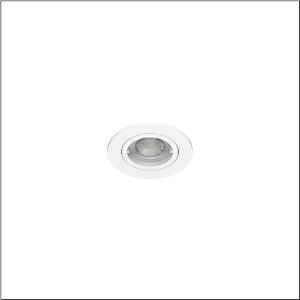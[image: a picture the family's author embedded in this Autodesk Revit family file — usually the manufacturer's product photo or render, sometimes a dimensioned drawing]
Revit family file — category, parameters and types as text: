
# Revit family: lunis_41_spot_51dt137a32a
name_source: partatom
category: Lighting Fixtures
units: mm (PartAtom-declared; Revit-internal decimal feet)

## family parameters
Cut with Voids When Loaded = No
Host = Face
Light Source = No
Part Type = Normal
Room Calculation Point = No
Round Connector Dimension = Use Diameter
Shared = No

## types (1)
- Lunis 41 Spot (1 x LED, 650 lm, 6.5 W, 3000K)
    Apparent Load = 7 VA
    CIE Flux Codes = 87 97 99 100 100
    Color Rendering = 80
    Color Temperature = 3000K
    Default Elevation = 1800 mm
    Description = Lunis 41,  Spot, downlight, light emission: direct distribution, LED rated luminous flux: 650lm, light colour: 830, control gear: ECG, mains connection: 230V, AC, 50/60Hz, housing, round, of aluminium, coated, traffic white (RAL 9016), diameter: 88mm, recess depth: 54mm, protection rating (complete): IP20, protection rating (on room side): IP20, insulation class (complete): insulation class II (safety insulation), certification: CE, permissible ambient temperature for indoor applications: -20..+40°C, packaging unit: 1 piece
    Height = 0 mm  [stored 0 ft]
    Lamp = 1 x LED
    Lamp Light Flux = 650 lm
    Lamp Power = 6.5 W
    Lamp count = 1
    Length = 88 mm
    Luminous efficacy = 100 lm/W
    Manufacturer = Siteco
    ModVariant = No
    Model = 51DT137A32A
    Mounting Place = Ceiling
    Mounting Type = Recessed
    Number of Poles = 1
    OnlyDefault = Yes
    Power Factor = 1
    Product Name = Lunis 41 Spot
    Product group = downlight
    ProductGroupID = 401
    Protection Class = Protection class II
    Protection Degree = IP 20
    RLX_Detail_Level = 1
    RLX_Emergency_Light_Flux = 0 lm
    RLX_Emergency_Type = 0
    RLX_Emergency_Type_DB = No
    RlxData = <blob elided: 37953 chars, md5=e2121855>
    Socket = socket
    Standby Power = 0 W
    System Light Flux = 650 lm
    System Power = 7 W
    Type Comments = Product without accessories
    Type Image = l_1005286.jpg
    URL = http://relux.com
    VarID = ---
    Voltage = 0 V
    Weight = 0.00 kg
    Width = 0 mm  [stored 0 ft]

note: [stored X ft] marks values corroborated as IEEE doubles in the binary element streams (Revit-internal decimal feet)

## geometry (parser evidence)
native form markers: Blend x4, Sweep x9
no freeform markers — native parametric forms only
